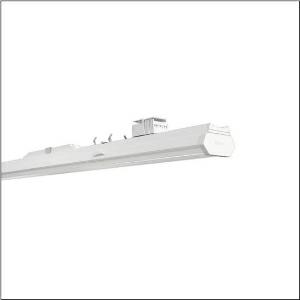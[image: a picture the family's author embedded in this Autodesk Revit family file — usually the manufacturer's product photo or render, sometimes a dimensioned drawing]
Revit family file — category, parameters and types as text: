
# Revit family: licross_r__11_protected_ho_51tp12dn5exl_83db
name_source: partatom
category: Lighting Fixtures
units: mm (PartAtom-declared; Revit-internal decimal feet)

## family parameters
Cut with Voids When Loaded = No
Host = Face
Light Source = No
Part Type = Normal
Room Calculation Point = No
Round Connector Dimension = Use Diameter
Shared = No

## types (1)
- --- (1 x LED, 14100 lm, 86.1 W, 5000K)
    Apparent Load = 86 VA
    CIE Flux Codes = 70 91 97 98 100
    Color Rendering = 80
    Color Temperature = 5000K
    Default Elevation = 1800 mm
    Description = Licross® 11 Protected HOluminaire insert, length: 1.500mm, width: 90mm, height: 101mm, LED rated luminous flux: 14.100lm, light colour: 850, control gear: DALI 2, control gear: ECG DALI, with plug, 5-pole, with phase selection, mains connection: 220..240V, AC, 50/60Hz, halogen-free wiring, primary optical cover: cover, of PMMA, light emission: direct with ceiling illumination distribution, protection rating (complete): IP64, insulation class (complete): insulation class I (protective earthing), certification: CE, ENEC, VDE, protection symbol: D if used in an environment with conductive dust loads with corresponding accessories, permissible ambient temperature for indoor applications: -25..+35°C, reducing of maximum allowable ambient temperature of 5°C with ceiling mounting, corresponds to IFS (International Featured Standards) requirements for safety and quality in the food industry, packaging unit: 1 piece
    Height = 92 mm
    Lamp = 1 x LED
    Lamp Light Flux = 14100 lm
    Lamp Power = 86.1 W
    Lamp count = 1
    Length = 1500 mm
    Luminous efficacy = 164 lm/W
    Manufacturer = Siteco
    ModVariant = No
    Model = 51TP12DN5EXL
    Mounting Place = Ceiling
    Mounting Type = Pendant
    Number of Poles = 1
    OnlyDefault = Yes
    Power Factor = 1
    Product Name = Licross® 11 Protected HO
    Product group = luminaire insert
    ProductGroupID = 902
    Protection Class = Protection class I
    Protection Degree = IP 64
    RLX_Detail_Level = 1
    RlxData = <blob elided: 24049 chars, md5=7bc6f451>
    Socket = socket
    Standby Power = 0 W
    System Light Flux = 14100 lm
    System Power = 86 W
    Type Comments = factory setting: luminous flux: 100 % | dim-lin: 254 | 485 mA
    Type Image = l_1256148.jpg
    URL = http://relux.com
    VarID = @adj_137969
    Voltage = 0 V
    Weight = 0.00 kg
    Width = 88 mm

## geometry (parser evidence)
native form markers: Blend x4, Sweep x12
no freeform markers — native parametric forms only
